# Revit family: anna_pendantlamp
name_source: partatom
category: Luminarias
units: mm (PartAtom-declared; Revit-internal decimal feet)

## family parameters
Compartido = No
Corte con vacíos al cargar = Sí
Cota de conector redondo = Diámetro de uso
Número OmniClass = 23.80.70.00
Origen de luz = No
Punto de cálculo de habitación = No
Se basa en plano de trabajo = Sí
Siempre vertical = No
Tipo de pieza = Normal
Título OmniClass = Lighting

## types (2) — shared parameters
Elevación por defecto = 1219 mm
FARO_Category = Indoor
FARO_Last Actualization Date = 13/12/2024
FARO_Material_02 = FARO_White_translucide
FARO_Model Line = ANNA
FARO_Subcategory = Suspended
Fabricante = FARO Barcelona
LAMP 1 = Sí
LAMP 2 = No
Lámpara = 1XE27 MAX 15W LED
URL = https://www.faro.es
Voltage = 100-240 V

## per-type parameters (varying)
| type | FARO_Description EN | FARO_Description ES | FARO_Material_01 | FARO_Ref |
| 22032 ANNA Black pendant lamp | ANNA Black pendant lamp | ANNA Colgante negro | FARO_Black_ | 22032 |
| 22033 ANNA White pendant lamp | ANNA white pendant lamp | ANNA Colgante blanco | FARO_White | 22033 |

## geometry (parser evidence)
native form markers: Sweep x9
no freeform markers — native parametric forms only
